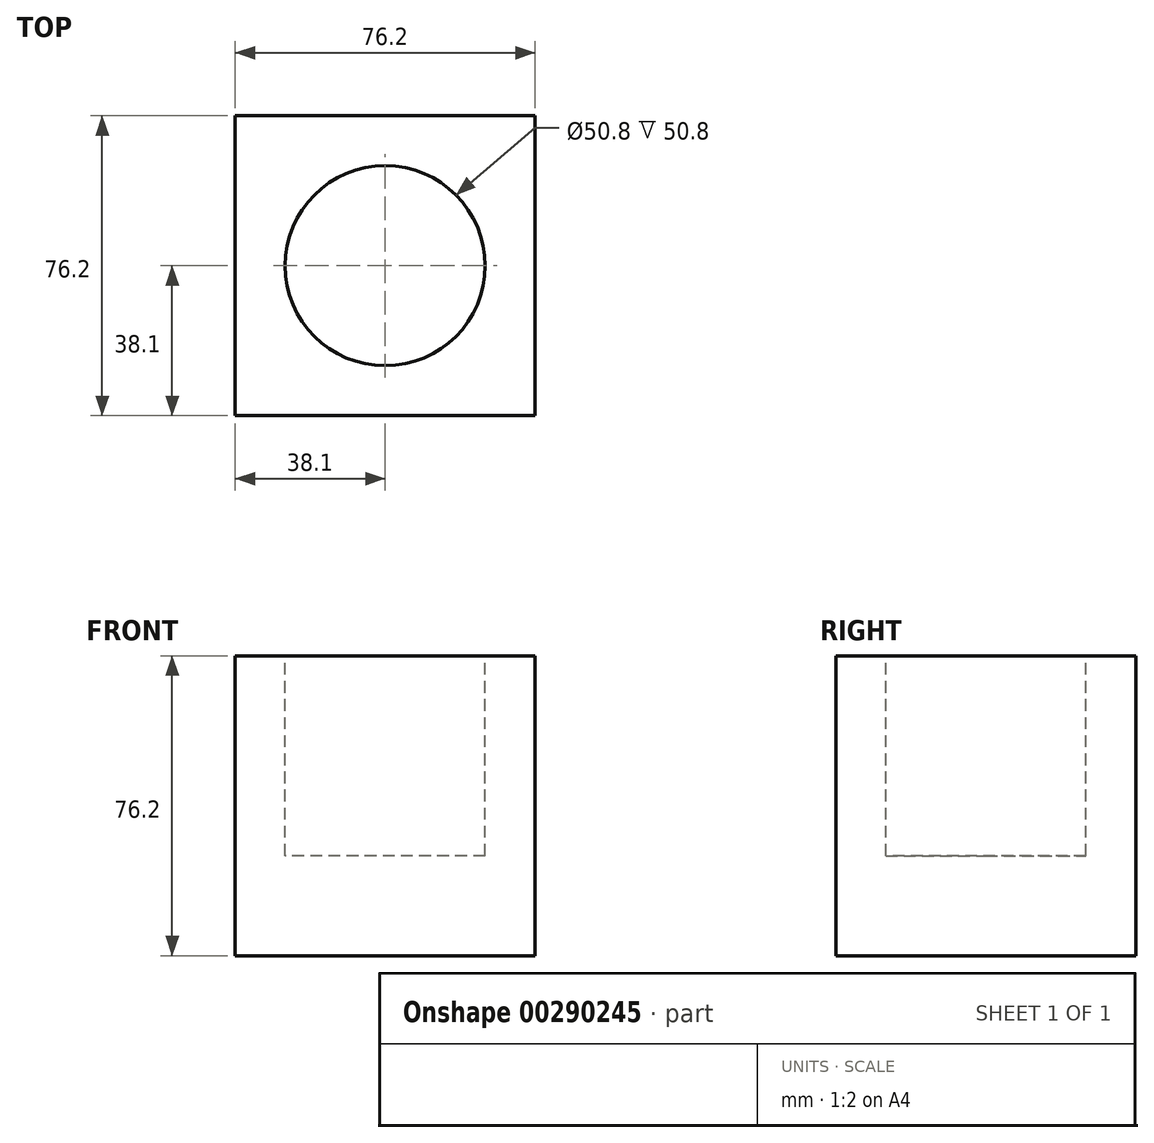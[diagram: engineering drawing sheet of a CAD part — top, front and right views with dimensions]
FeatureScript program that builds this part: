
annotation { "Feature Type Name" : "Feature", "Feature Type Description" : "" }
export const myFeature = defineFeature(function(context is Context, id is Id, definition is map)
    precondition{}
    {
        {
            var Q0;
            Q0=qCreatedBy(makeId("Top.planeOp"),FACE);
            var sketch = newSketch(context, id + "F0", { "sketchPlane" : qUnion([Q0])});
            skLineSegment(sketch, "E0.bottom", {"start": v(0, 0) * mm, "end": v(-76.2, 0) * mm});
            skLineSegment(sketch, "E0.top", {"start": v(0, 76.2) * mm, "end": v(-76.2, 76.2) * mm});
            skLineSegment(sketch, "E0.left", {"start": v(0, 0) * mm, "end": v(0, 76.2) * mm});
            skLineSegment(sketch, "E0.right", {"start": v(-76.2, 0) * mm, "end": v(-76.2, 76.2) * mm});
            skPoint(sketch, "E1.center.orphan", {"position": v(-38.1, 38.1) * mm});
            skSolve(sketch);
        }
        {
            var Q0;
            Q0=makeQuery(id+"F0.imprint","IMPRINT",FACE,{"disambiguationData":[TD([[makeQuery(id+"F0.imprint","IMPRINT",EDGE,{"derivedFrom":sQuery(id+"F0.wireOp",EDGE,"E0.bottom")}),-1.0]])]});
            extrude(context, id + "F1", {"entities" : qUnion([Q0]), "depth" : 76.2 * mm});
        }
        {
            var Q0;
            Q0=makeQuery(id+"F1.opExtrude","CAP_FACE",FACE,{"disambiguationData":[OSD([sQuery(id+"F0.wireOp",EDGE,"E0.bottom"),sQuery(id+"F0.wireOp",EDGE,"E0.top"),sQuery(id+"F0.wireOp",EDGE,"E0.left"),sQuery(id+"F0.wireOp",EDGE,"E0.right")])],"isStart":false});
            var sketch = newSketch(context, id + "F2", { "sketchPlane" : qUnion([Q0])});
            skCircle(sketch, "E2", {"center": v(-38.1, 38.1) * mm, "radius": 25.4 * mm});
            skSolve(sketch);
        }
        {
            var Q0;
            Q0=makeQuery(id+"F2.imprint","IMPRINT",FACE,{"disambiguationData":[TD([[makeQuery(id+"F2.imprint","IMPRINT",EDGE,{"derivedFrom":sQuery(id+"F2.wireOp",EDGE,"E2")}),1.0]])]});
            extrude(context, id + "F3", {"entities" : qUnion([Q0]), "operationType" : NewBodyOperationType.REMOVE, "oppositeDirection" : true, "depth" : 50.8 * mm});
        }
    });
